# Revit family: AVAD_Upblast_Ceiling_Mount
name_source: partatom
category: Mechanical Equipment
units: mm (PartAtom-declared; Revit-internal decimal feet)

## family parameters
Always vertical = Yes
Cut with Voids When Loaded = No
Part Type = Normal
Room Calculation Point = No
Round Connector Dimension = Use Radius
Shared = No
Work Plane-Based = No

## types (8) — shared parameters
0 = 0' - 0"
1" = 0' - 1"
1.5 = 0' - 1 1/2"
2" = 0' - 2"
2' = 2' - 0"
3" = 0' - 3"
30 = 30.00°
4" = 0' - 4"
45 = 45.00°
60 = 60.00°
Manufacturer = Loren Cook Company
Model = AVAD
ONE EIGTH = 0' - 0 1/8"
Type Comments = Adjustable Pitch Vane Axial Upblast Ceiling Mount Direct Drive Arrangement 4
URL = www.lorencook.com

## per-type parameters (varying)
- 35_AVAD_UPBLAST_CEILING: (A+.25")/2=1' - 5 7/8"; (E-.25")/2=1' - 2 7/8"; (J+(J-B))/2=1' - 11 3/16"; (J-B)/2=0' - 1 5/8"; (L/2)-1"=1' - 2 1/4"; -(E-.25")/2=-1' - 2 7/8"; -E/2=-1' - 3"; A=2' - 11 1/2"; A/2=1' - 5 3/4"; A/3=1' - 2 3/16"; B=3' - 3 7/8"; B/2=1' - 7 15/16"; C=3' - 2"; C/2=1' - 7"; E=2' - 6"; E-.125"=2' - 5 7/8"; E-2"=2' - 4"; E/2=1' - 3"; F=0' - 0 9/16"; F/2=0' - 0 9/32"; G=12' - 0"; H=3' - 11 7/8"; J=3' - 7 1/8"; J-B=0' - 3 1/4"; J/2=1' - 9 9/16"; K=0' - 0 9/16"; K/2=0' - 0 9/32"; L=2' - 6 1/2"; L/2=1' - 3 1/4"
- 39_AVAD_UPBLAST_CEILING: (A+.25")/2=1' - 7 13/16"; (E-.25")/2=1' - 2 7/8"; (J+(J-B))/2=2' - 1 5/32"; (J-B)/2=0' - 1 19/32"; (L/2)-1"=1' - 3 21/32"; -(E-.25")/2=-1' - 2 7/8"; -E/2=-1' - 3"; A=3' - 3 3/8"; A/2=1' - 7 11/16"; A/3=1' - 3 3/4"; B=3' - 7 15/16"; B/2=1' - 9 31/32"; C=3' - 5 7/8"; C/2=1' - 8 15/16"; E=2' - 6"; E-.125"=2' - 5 7/8"; E-2"=2' - 4"; E/2=1' - 3"; F=0' - 0 9/16"; F/2=0' - 0 9/32"; G=12' - 0"; H=4' - 1 7/8"; J=3' - 11 1/8"; J-B=0' - 3 3/16"; J/2=1' - 11 9/16"; K=0' - 0 9/16"; K/2=0' - 0 9/32"; L=2' - 9 5/16"; L/2=1' - 4 21/32"
- 44_AVAD_UPBLAST_CEILING: (A+.25")/2=1' - 10 3/16"; (E-.25")/2=1' - 4 7/8"; (J+(J-B))/2=2' - 5 1/16"; (J-B)/2=0' - 2 1/8"; (L/2)-1"=1' - 6 1/16"; -(E-.25")/2=-1' - 4 7/8"; -E/2=-1' - 5"; A=3' - 8 1/8"; A/2=1' - 10 1/16"; A/3=1' - 5 21/32"; B=4' - 1 5/8"; B/2=2' - 0 13/16"; C=3' - 11 3/8"; C/2=1' - 11 11/16"; E=2' - 10"; E-.125"=2' - 9 7/8"; E-2"=2' - 8"; E/2=1' - 5"; F=0' - 0 9/16"; F/2=0' - 0 9/32"; G=12' - 0"; H=4' - 5 1/4"; J=4' - 5 7/8"; J-B=0' - 4 1/4"; J/2=2' - 2 15/16"; K=0' - 0 11/16"; K/2=0' - 0 11/32"; L=3' - 2 1/8"; L/2=1' - 7 1/16"
- 49_AVAD_UPBLAST_CEILING: (A+.25")/2=2' - 0 3/4"; (E-.25")/2=1' - 4 7/8"; (J+(J-B))/2=2' - 7 5/8"; (J-B)/2=0' - 2 1/8"; (L/2)-1"=1' - 7 7/8"; -(E-.25")/2=-1' - 4 7/8"; -E/2=-1' - 5"; A=4' - 1 1/4"; A/2=2' - 0 5/8"; A/3=1' - 7 11/16"; B=4' - 6 3/4"; B/2=2' - 3 3/8"; C=4' - 4 1/2"; C/2=2' - 2 1/4"; E=2' - 10"; E-.125"=2' - 9 7/8"; E-2"=2' - 8"; E/2=1' - 5"; F=0' - 0 9/16"; F/2=0' - 0 9/32"; G=12' - 0"; H=4' - 7 3/4"; J=4' - 11"; J-B=0' - 4 1/4"; J/2=2' - 5 1/2"; K=0' - 0 11/16"; K/2=0' - 0 11/32"; L=3' - 5 3/4"; L/2=1' - 8 7/8"
- 57_AVAD_UPBLAST_CEILING: (A+.25")/2=2' - 4 11/16"; (E-.25")/2=1' - 8 7/8"; (J+(J-B))/2=2' - 11 9/16"; (J-B)/2=0' - 2 1/8"; (L/2)-1"=1' - 10 21/32"; -(E-.25")/2=-1' - 8 7/8"; -E/2=-1' - 9"; A=4' - 9 1/8"; A/2=2' - 4 9/16"; A/3=1' - 10 27/32"; B=5' - 2 5/8"; B/2=2' - 7 5/16"; C=4' - 11 7/8"; C/2=2' - 5 15/16"; E=3' - 6"; E-.125"=3' - 5 7/8"; E-2"=3' - 4"; E/2=1' - 9"; F=0' - 0 9/16"; F/2=0' - 0 9/32"; G=12' - 0"; H=5' - 5 3/4"; J=5' - 6 7/8"; J-B=0' - 4 1/4"; J/2=2' - 9 7/16"; K=0' - 0 11/16"; K/2=0' - 0 11/32"; L=3' - 11 5/16"; L/2=1' - 11 21/32"
- 63_AVAD_UPBLAST_CEILING: (A+.25")/2=2' - 7 5/8"; (E-.25")/2=1' - 8 7/8"; (J+(J-B))/2=3' - 2 1/2"; (J-B)/2=0' - 2 1/8"; (L/2)-1"=2' - 0 23/32"; -(E-.25")/2=-1' - 8 7/8"; -E/2=-1' - 9"; A=5' - 3"; A/2=2' - 7 1/2"; A/3=2' - 1 3/16"; B=5' - 8 1/2"; B/2=2' - 10 1/4"; C=5' - 6 1/4"; C/2=2' - 9 1/8"; E=3' - 6"; E-.125"=3' - 5 7/8"; E-2"=3' - 4"; E/2=1' - 9"; F=0' - 0 11/16"; F/2=0' - 0 11/32"; G=16' - 0"; H=5' - 8 5/8"; J=6' - 0 3/4"; J-B=0' - 4 1/4"; J/2=3' - 0 3/8"; K=0' - 0 11/16"; K/2=0' - 0 11/32"; L=4' - 3 7/16"; L/2=2' - 1 23/32"
- 71_AVAD_UPBLAST_CEILING: (A+.25")/2=2' - 11 9/16"; (E-.25")/2=2' - 2 7/8"; (J+(J-B))/2=3' - 7 13/16"; (J-B)/2=0' - 2 1/2"; (L/2)-1"=2' - 4 7/32"; -(E-.25")/2=-2' - 2 7/8"; -E/2=-2' - 3"; A=5' - 10 7/8"; A/2=2' - 11 7/16"; A/3=2' - 4 11/32"; B=6' - 5 5/8"; B/2=3' - 2 13/16"; C=6' - 3"; C/2=3' - 1 1/2"; E=4' - 6"; E-.125"=4' - 5 7/8"; E-2"=4' - 4"; E/2=2' - 3"; F=0' - 0 11/16"; F/2=0' - 0 11/32"; G=16' - 0"; H=6' - 0 3/4"; J=6' - 10 5/8"; J-B=0' - 5"; J/2=3' - 5 5/16"; K=0' - 0 11/16"; K/2=0' - 0 11/32"; L=4' - 10 7/16"; L/2=2' - 5 7/32"
- 79_AVAD_UPBLAST_CEILING: (A+.25")/2=3' - 3 1/2"; (E-.25")/2=2' - 2 7/8"; (J+(J-B))/2=3' - 11 23/32"; (J-B)/2=0' - 2 15/32"; (L/2)-1"=2' - 7"; -(E-.25")/2=-2' - 2 7/8"; -E/2=-2' - 3"; A=6' - 6 3/4"; A/2=3' - 3 3/8"; A/3=2' - 7 1/2"; B=7' - 1 9/16"; B/2=3' - 6 25/32"; C=6' - 10 7/8"; C/2=3' - 5 7/16"; E=4' - 6"; E-.125"=4' - 5 7/8"; E-2"=4' - 4"; E/2=2' - 3"; F=0' - 0 11/16"; F/2=0' - 0 11/32"; G=16' - 0"; H=6' - 4 5/8"; J=7' - 6 1/2"; J-B=0' - 4 15/16"; J/2=3' - 9 1/4"; K=0' - 0 11/16"; K/2=0' - 0 11/32"; L=5' - 4"; L/2=2' - 8"

## geometry (parser evidence)
native form markers: Sweep x2
no freeform markers — native parametric forms only
